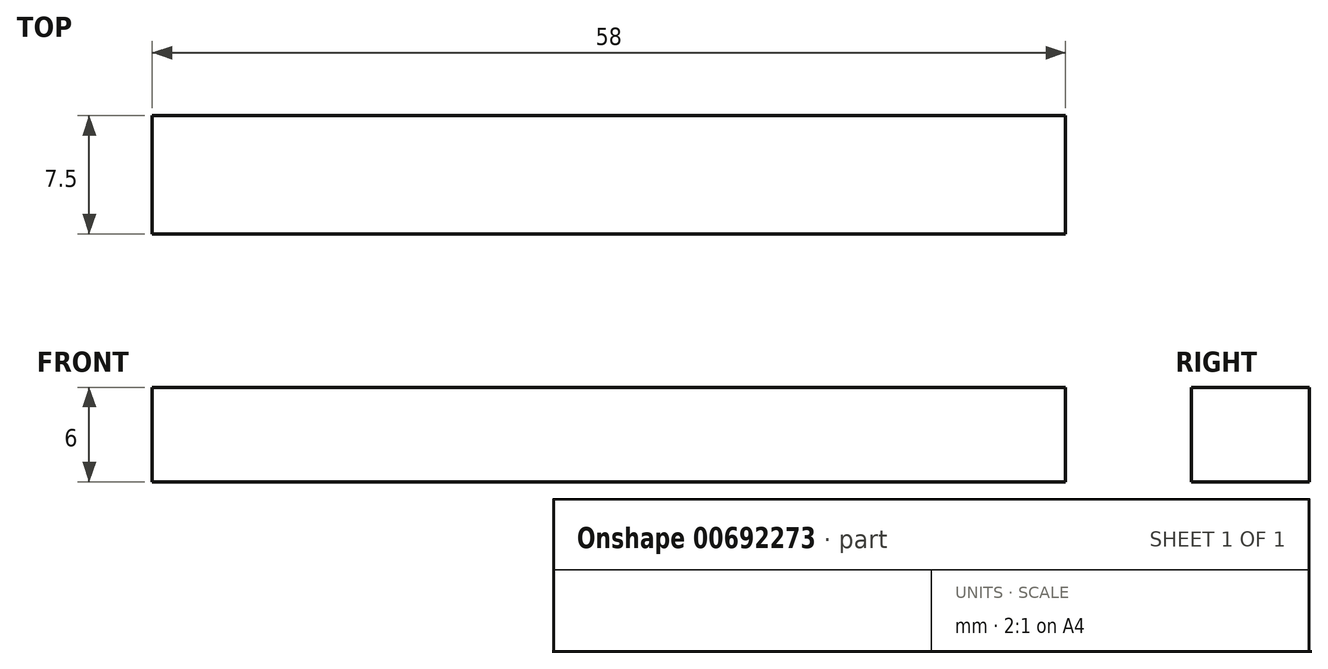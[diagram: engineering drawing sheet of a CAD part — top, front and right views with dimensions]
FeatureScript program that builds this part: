
annotation { "Feature Type Name" : "Feature", "Feature Type Description" : "" }
export const myFeature = defineFeature(function(context is Context, id is Id, definition is map)
    precondition{}
    {
        {
            var Q0;
            Q0=qCreatedBy(makeId("Top.planeOp"),FACE);
            var sketch = newSketch(context, id + "F0", { "sketchPlane" : qUnion([Q0])});
            skLineSegment(sketch, "E0.bottom", {"start": v(0, 0) * mm, "end": v(58, 0) * mm});
            skLineSegment(sketch, "E0.top", {"start": v(0, 7.5) * mm, "end": v(58, 7.5) * mm});
            skLineSegment(sketch, "E0.left", {"start": v(0, 0) * mm, "end": v(0, 7.5) * mm});
            skLineSegment(sketch, "E0.right", {"start": v(58, 0) * mm, "end": v(58, 7.5) * mm});
            skSolve(sketch);
        }
        {
            var Q0;
            Q0 = qSketchRegion(id + "F0", true);
            extrude(context, id + "F1", {"entities" : qUnion([Q0]), "depth" : 6 * mm, "offsetDistance" : 25.4 * mm});
        }
    });
